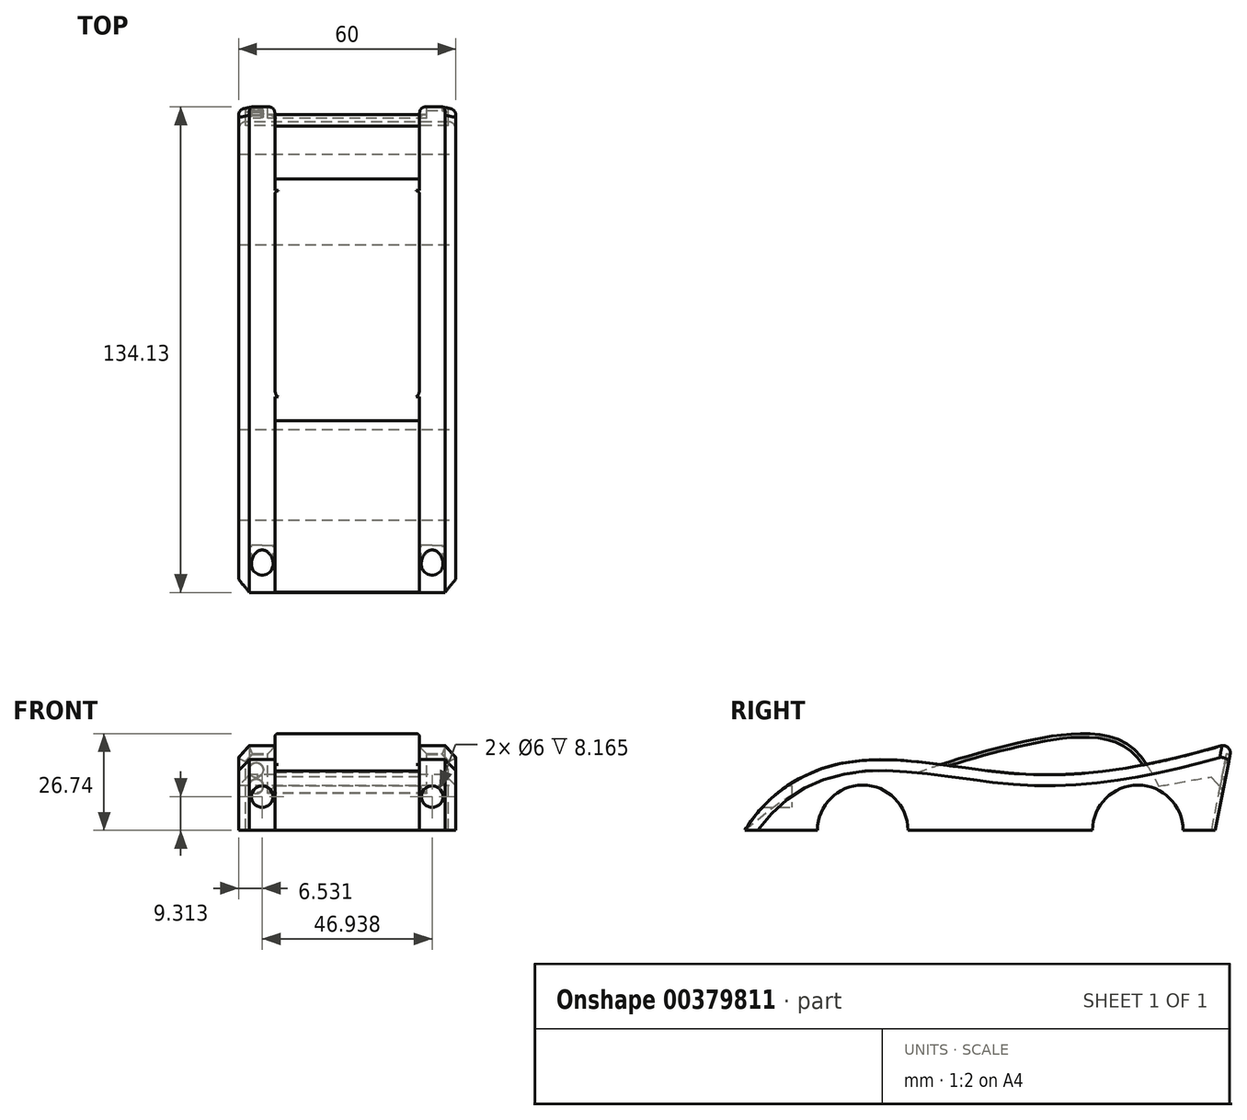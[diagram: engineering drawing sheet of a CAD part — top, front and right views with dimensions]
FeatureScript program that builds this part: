
annotation { "Feature Type Name" : "Feature", "Feature Type Description" : "" }
export const myFeature = defineFeature(function(context is Context, id is Id, definition is map)
    precondition{}
    {
        {
            var Q0;
            Q0=qCreatedBy(makeId("Right.planeOp"),FACE);
            var sketch = newSketch(context, id + "F0", { "sketchPlane" : qUnion([Q0])});
            skLineSegment(sketch, "E0", {"start": v(-69.96, 0) * mm, "end": v(60.04, 0) * mm});
            skLineSegment(sketch, "E1", {"start": v(60.04, 0) * mm, "end": v(64.77, 24.27) * mm});
            skFitSpline(sketch, "E2", {"points": [v(-69.96, 0) * mm, v(-38.45, 19.22) * mm, v(8.82, 15.44) * mm, v(64.77, 24.27) * mm], "startDerivative": vector(75.95, 120.9) * mm, "endDerivative": vector(158.07, 47.6) * mm});
            skSolve(sketch);
        }
        {
            var Q0;
            Q0 = qSketchRegion(id + "F0", true);
            extrude(context, id + "F1", {"entities" : qUnion([Q0]), "endBound" : BoundingType.SYMMETRIC, "depth" : 60 * mm});
        }
        {
            var Q0;
            Q0=qCreatedBy(makeId("Right.planeOp"),FACE);
            var sketch = newSketch(context, id + "F2", { "sketchPlane" : qUnion([Q0])});
            skFitSpline(sketch, "E3", {"points": [v(-69.97, 0) * mm, v(-53.13, 11.86) * mm, v(-31.07, 16.37) * mm, v(-7.6, 13.52) * mm], "startDerivative": vector(49.2, 41.7) * mm, "endDerivative": vector(68.07, -12.52) * mm});
            skLineSegment(sketch, "E4", {"start": v(-69.97, 0) * mm, "end": v(-69.97, 23.96) * mm});
            skLineSegment(sketch, "E5", {"start": v(-69.97, 23.96) * mm, "end": v(-35.1, 31.55) * mm});
            skLineSegment(sketch, "E6", {"start": v(-35.1, 31.55) * mm, "end": v(0, 20.64) * mm});
            skLineSegment(sketch, "E7", {"start": v(0, 20.64) * mm, "end": v(-7.6, 13.52) * mm});
            skLineSegment(sketch, "E8", {"start": v(17.32, 20.64) * mm, "end": v(66.9, 28.23) * mm});
            skFitSpline(sketch, "E9", {"points": [v(17.32, 20.64) * mm, v(24.2, 15.06) * mm, v(39.14, 11.62) * mm, v(65.82, 14.59) * mm, v(68.79, 9.84) * mm], "startDerivative": vector(30.48, -28.51) * mm, "endDerivative": vector(7.56, -36.36) * mm});
            skLineSegment(sketch, "E10", {"start": v(66.9, 28.23) * mm, "end": v(65.82, 14.59) * mm});
            skSolve(sketch);
        }
        {
            var Q0;
            Q0=makeQuery(id+"F2.imprint","IMPRINT",FACE,{"disambiguationData":[TD([[makeQuery(id+"F2.imprint","IMPRINT",EDGE,{"derivedFrom":sQuery(id+"F2.wireOp",EDGE,"E3")}),1.0]])]});
            var Q1;
            {var subQ0=sQuery(id+"F2.wireOp",EDGE,"E8");Q1=makeQuery(id+"F2.imprint","IMPRINT",FACE,{"disambiguationData":[TD([[makeQuery(id+"F2.imprint","IMPRINT",EDGE,{"derivedFrom":subQ0}),-1.0]])]});}
            extrude(context, id + "F3", {"entities" : qUnion([Q0, Q1]), "operationType" : NewBodyOperationType.REMOVE, "endBound" : BoundingType.SYMMETRIC, "depth" : 40 * mm});
        }
        {
            var Q0;
            Q0=qCreatedBy(makeId("Right.planeOp"),FACE);
            var sketch = newSketch(context, id + "F4", { "sketchPlane" : qUnion([Q0])});
            skFitSpline(sketch, "E11", {"points": [v(-24.28, 15.25) * mm, v(3.4, 23.64) * mm, v(35.77, 23.8) * mm, v(46.97, 6.64) * mm], "startDerivative": vector(69.15, 25.57) * mm, "endDerivative": vector(25.04, -44.14) * mm});
            skLineSegment(sketch, "E12", {"start": v(-24.28, 15.25) * mm, "end": v(46.97, 6.64) * mm});
            skSolve(sketch);
        }
        {
            var Q0;
            Q0=makeQuery(id+"F4.imprint","IMPRINT",FACE,{"disambiguationData":[TD([[makeQuery(id+"F4.imprint","IMPRINT",EDGE,{"derivedFrom":sQuery(id+"F4.wireOp",EDGE,"E11")}),-1.0]])]});
            extrude(context, id + "F5", {"entities" : qUnion([Q0]), "operationType" : NewBodyOperationType.ADD, "endBound" : BoundingType.SYMMETRIC, "depth" : 40 * mm});
        }
        {
            var Q0;
            Q0=makeQuery(id+"F1.opExtrude","CAP_EDGE",EDGE,{"disambiguationData":[OSD([sQuery(id+"F0.wireOp",EDGE,"E2")])],"isStart":false});
            var Q1;
            Q1=makeQuery(id+"F1.opExtrude","CAP_EDGE",EDGE,{"disambiguationData":[OSD([sQuery(id+"F0.wireOp",EDGE,"E2")])],"isStart":true});
            var Q2;
            Q2=makeQuery(id+"F3.boolean.opBoolean","INTERSECT",EDGE,{"derivedFrom":[makeQuery(id+"F1.opExtrude","SWEPT_FACE",FACE,{"disambiguationData":[OSD([sQuery(id+"F0.wireOp",EDGE,"E1")])]}),makeQuery(id+"F3.opExtrude","SWEPT_FACE",FACE,{"disambiguationData":[OSD([sQuery(id+"F2.wireOp",EDGE,"E9")])]})]});
            chamfer(context, id + "F6", {"entities" : qUnion([Q0, Q1, Q2]), "width" : 3 * mm, "tangentPropagation" : true});
        }
        {
            var Q0;
            Q0=makeQuery(id+"F3.boolean.opBoolean","INTERSECT",EDGE,{"derivedFrom":[makeQuery(id+"F1.opExtrude","SWEPT_FACE",FACE,{"disambiguationData":[OSD([sQuery(id+"F0.wireOp",EDGE,"E1")])]}),makeQuery(id+"F3.opExtrude","CAP_FACE",FACE,{"disambiguationData":[OSD([sQuery(id+"F2.wireOp",EDGE,"E8"),sQuery(id+"F2.wireOp",EDGE,"E9"),sQuery(id+"F2.wireOp",EDGE,"E10")])],"isStart":false})]});
            var Q1;
            Q1=makeQuery(id+"F3.boolean.opBoolean","INTERSECT",EDGE,{"derivedFrom":[makeQuery(id+"F1.opExtrude","SWEPT_FACE",FACE,{"disambiguationData":[OSD([sQuery(id+"F0.wireOp",EDGE,"E1")])]}),makeQuery(id+"F3.opExtrude","CAP_FACE",FACE,{"disambiguationData":[OSD([sQuery(id+"F2.wireOp",EDGE,"E8"),sQuery(id+"F2.wireOp",EDGE,"E9"),sQuery(id+"F2.wireOp",EDGE,"E10")])],"isStart":true})]});
            var Q2;
            Q2=makeQuery(id+"F6.opChamfer","BLEND_EDGE",EDGE,{"blendedFrom":[makeQuery(id+"F1.opExtrude","CAP_EDGE",EDGE,{"disambiguationData":[OSD([sQuery(id+"F0.wireOp",EDGE,"E2")])],"isStart":true}),makeQuery(id+"F1.opExtrude","SWEPT_FACE",FACE,{"disambiguationData":[OSD([sQuery(id+"F0.wireOp",EDGE,"E1")])]})],"blendedInto":[makeQuery(id+"F1.opExtrude","SWEPT_FACE",FACE,{"disambiguationData":[OSD([sQuery(id+"F0.wireOp",EDGE,"E1")])]})]});
            var Q3;
            {var subQ0=sQuery(id+"F0.wireOp",EDGE,"E2");var subQ1=sQuery(id+"F0.wireOp",EDGE,"E1");Q3=makeQuery(id+"F3.boolean.opBoolean","SPLIT",EDGE,{"disambiguationData":[TD([makeQuery(id+"F3.opExtrude","CAP_FACE",FACE,{"disambiguationData":[OSD([sQuery(id+"F2.wireOp",EDGE,"E8"),sQuery(id+"F2.wireOp",EDGE,"E9"),sQuery(id+"F2.wireOp",EDGE,"E10")])],"isStart":true})])],"derivedFrom":makeQuery(id+"F1.opExtrude","SWEPT_EDGE",EDGE,{"disambiguationData":[OSD([subQ1,subQ0])]})});}
            var Q4;
            {var subQ0=sQuery(id+"F0.wireOp",EDGE,"E2");var subQ1=sQuery(id+"F0.wireOp",EDGE,"E1");Q4=makeQuery(id+"F3.boolean.opBoolean","SPLIT",EDGE,{"disambiguationData":[TD([makeQuery(id+"F3.opExtrude","CAP_FACE",FACE,{"disambiguationData":[OSD([sQuery(id+"F2.wireOp",EDGE,"E8"),sQuery(id+"F2.wireOp",EDGE,"E9"),sQuery(id+"F2.wireOp",EDGE,"E10")])],"isStart":false})])],"derivedFrom":makeQuery(id+"F1.opExtrude","SWEPT_EDGE",EDGE,{"disambiguationData":[OSD([subQ1,subQ0])]})});}
            var Q5;
            Q5=makeQuery(id+"F6.opChamfer","BLEND_EDGE",EDGE,{"blendedFrom":[makeQuery(id+"F1.opExtrude","CAP_EDGE",EDGE,{"disambiguationData":[OSD([sQuery(id+"F0.wireOp",EDGE,"E2")])],"isStart":false}),makeQuery(id+"F1.opExtrude","SWEPT_FACE",FACE,{"disambiguationData":[OSD([sQuery(id+"F0.wireOp",EDGE,"E1")])]})],"blendedInto":[makeQuery(id+"F1.opExtrude","SWEPT_FACE",FACE,{"disambiguationData":[OSD([sQuery(id+"F0.wireOp",EDGE,"E1")])]})]});
            var Q6;
            {var subQ0=makeQuery(id+"F1.opExtrude","SWEPT_FACE",FACE,{"disambiguationData":[OSD([sQuery(id+"F0.wireOp",EDGE,"E1")])]});Q6=makeQuery(id+"F6.opChamfer","BLEND_EDGE",EDGE,{"blendedFrom":[makeQuery(id+"F3.boolean.opBoolean","INTERSECT",EDGE,{"derivedFrom":[subQ0,makeQuery(id+"F3.opExtrude","SWEPT_FACE",FACE,{"disambiguationData":[OSD([sQuery(id+"F2.wireOp",EDGE,"E9")])]})]}),subQ0],"blendedInto":[subQ0]});}
            var Q7;
            Q7=makeQuery(id+"F1.opExtrude","CAP_EDGE",EDGE,{"disambiguationData":[OSD([sQuery(id+"F0.wireOp",EDGE,"E1")])],"isStart":true});
            var Q8;
            Q8=makeQuery(id+"F1.opExtrude","CAP_EDGE",EDGE,{"disambiguationData":[OSD([sQuery(id+"F0.wireOp",EDGE,"E1")])],"isStart":false});
            fillet(context, id + "F7", {"entities" : qUnion([Q0, Q1, Q2, Q3, Q4, Q5, Q6, Q7, Q8]), "radius" : 2 * mm, "tangentPropagation" : true, "allowEdgeOverflow" : false});
        }
        {
            var Q0;
            {var subQ0=sQuery(id+"F4.wireOp",EDGE,"E11");Q0=makeQuery(id+"F5.boolean.opBoolean","SPLIT",EDGE,{"disambiguationData":[topologyDisambiguationEdgeConnected([makeQuery(id+"F5.opExtrude","CAP_FACE",FACE,{"disambiguationData":[OSD([subQ0,sQuery(id+"F4.wireOp",EDGE,"E12")])],"isStart":true})])],"derivedFrom":makeQuery(id+"F5.opExtrude","CAP_EDGE",EDGE,{"disambiguationData":[OSD([subQ0])],"isStart":true})});}
            var Q1;
            {var subQ0=sQuery(id+"F4.wireOp",EDGE,"E11");Q1=makeQuery(id+"F5.boolean.opBoolean","SPLIT",EDGE,{"disambiguationData":[topologyDisambiguationEdgeConnected([makeQuery(id+"F5.opExtrude","CAP_FACE",FACE,{"disambiguationData":[OSD([subQ0,sQuery(id+"F4.wireOp",EDGE,"E12")])],"isStart":false})])],"derivedFrom":makeQuery(id+"F5.opExtrude","CAP_EDGE",EDGE,{"disambiguationData":[OSD([subQ0])],"isStart":false})});}
            fillet(context, id + "F8", {"entities" : qUnion([Q0, Q1]), "radius" : 1 * mm, "tangentPropagation" : true, "allowEdgeOverflow" : false});
        }
        {
            var Q0;
            Q0=qCreatedBy(makeId("Right.planeOp"),FACE);
            var sketch = newSketch(context, id + "F9", { "sketchPlane" : qUnion([Q0])});
            skCircle(sketch, "E13", {"center": v(-37.4, 0) * mm, "radius": 12.5 * mm});
            skCircle(sketch, "E14", {"center": v(38.62, 0) * mm, "radius": 12.5 * mm});
            skSolve(sketch);
        }
        {
            var Q0;
            Q0=makeQuery(id+"F9.imprint","IMPRINT",FACE,{"disambiguationData":[TD([[makeQuery(id+"F9.imprint","IMPRINT",EDGE,{"derivedFrom":sQuery(id+"F9.wireOp",EDGE,"E13")}),1.0]])]});
            var Q1;
            Q1=makeQuery(id+"F9.imprint","IMPRINT",FACE,{"disambiguationData":[TD([[makeQuery(id+"F9.imprint","IMPRINT",EDGE,{"derivedFrom":sQuery(id+"F9.wireOp",EDGE,"E14")}),1.0]])]});
            extrude(context, id + "F10", {"entities" : qUnion([Q0, Q1]), "operationType" : NewBodyOperationType.REMOVE, "endBound" : BoundingType.SYMMETRIC, "oppositeDirection" : true, "depth" : 100 * mm});
        }
        {
            var Q0;
            Q0=qCreatedBy(makeId("Front.planeOp"),FACE);
            cPlane(context, id + "F11", {"entities" : qUnion([Q0]), "cplaneType" : CPlaneType.OFFSET, "offset" : 57 * mm, "width" : 150 * mm, "height" : 150 * mm});
        }
        {
            var Q0;
            Q0=qCreatedBy(id+"F11.planeOp",FACE);
            var sketch = newSketch(context, id + "F12", { "sketchPlane" : qUnion([Q0])});
            skCircle(sketch, "E15", {"center": v(-23.47, 9.31) * mm, "radius": 3 * mm});
            skCircle(sketch, "E16.MirrorC", {"center": v(23.47, 9.31) * mm, "radius": 3 * mm});
            skSolve(sketch);
        }
        {
            var Q0;
            Q0 = qSketchRegion(id + "F12", true);
            var Q1;
            Q1=makeQuery(id+"F1.opExtrude","SWEPT_BODY",BODY,{"disambiguationData":[OSD([sQuery(id+"F0.wireOp",EDGE,"E0"),sQuery(id+"F0.wireOp",EDGE,"E1"),sQuery(id+"F0.wireOp",EDGE,"E2")])]});
            extrude(context, id + "F13", {"entities" : qUnion([Q0]), "operationType" : NewBodyOperationType.REMOVE, "endBoundEntityBody" : qUnion([Q1]), "depth" : 15.4 * mm});
        }
        {
            var Q0;
            Q0=makeQuery(id+"F1.opExtrude","SWEPT_FACE",FACE,{"disambiguationData":[OSD([sQuery(id+"F0.wireOp",EDGE,"E1")])]});
            var sketch = newSketch(context, id + "F14", { "sketchPlane" : qUnion([Q0])});
            skLineSegment(sketch, "E17.bottom", {"start": v(9.73, 14.62) * mm, "end": v(-9.73, 14.62) * mm});
            skLineSegment(sketch, "E17.top", {"start": v(9.73, 19.94) * mm, "end": v(-9.73, 19.94) * mm});
            skLineSegment(sketch, "E17.left", {"start": v(9.73, 14.62) * mm, "end": v(9.73, 19.94) * mm});
            skLineSegment(sketch, "E17.right", {"start": v(-9.73, 14.62) * mm, "end": v(-9.73, 19.94) * mm});
            skPoint(sketch, "E17.middle", {"position": v(0, 17.28) * mm});
            skSolve(sketch);
        }
        {
            var Q0;
            Q0=makeQuery(id+"F14.imprint","IMPRINT",FACE,{"disambiguationData":[TD([[makeQuery(id+"F14.imprint","IMPRINT",EDGE,{"derivedFrom":sQuery(id+"F14.wireOp",EDGE,"E17.bottom")}),-1.0]])]});
            extrude(context, id + "F15", {"entities" : qUnion([Q0]), "operationType" : NewBodyOperationType.REMOVE, "oppositeDirection" : true, "depth" : 1 * mm});
        }
        {
            var Q0;
            Q0=makeQuery(id+"F1.opExtrude","SWEPT_FACE",FACE,{"disambiguationData":[OSD([sQuery(id+"F0.wireOp",EDGE,"E1")])]});
            var sketch = newSketch(context, id + "F16", { "sketchPlane" : qUnion([Q0])});
            skCircle(sketch, "E18", {"center": v(-25.14, 28.4) * mm, "radius": 2 * mm});
            skCircle(sketch, "E19", {"center": v(-25.14, 23.81) * mm, "radius": 2 * mm});
            skCircle(sketch, "E20.MirrorC", {"center": v(25.14, 28.4) * mm, "radius": 2 * mm});
            skCircle(sketch, "E21.MirrorC", {"center": v(25.14, 23.81) * mm, "radius": 2 * mm});
            skSolve(sketch);
        }
        {
            var Q0;
            Q0=makeQuery(id+"F16.imprint","IMPRINT",FACE,{"disambiguationData":[TD([[makeQuery(id+"F16.imprint","IMPRINT",EDGE,{"derivedFrom":sQuery(id+"F16.wireOp",EDGE,"E18")}),1.0]])]});
            var Q1;
            Q1=makeQuery(id+"F16.imprint","IMPRINT",FACE,{"disambiguationData":[TD([[makeQuery(id+"F16.imprint","IMPRINT",EDGE,{"derivedFrom":sQuery(id+"F16.wireOp",EDGE,"E19")}),1.0]])]});
            var Q2;
            Q2=makeQuery(id+"F16.imprint","IMPRINT",FACE,{"disambiguationData":[TD([[makeQuery(id+"F16.imprint","IMPRINT",EDGE,{"derivedFrom":sQuery(id+"F16.wireOp",EDGE,"E20.MirrorC")}),-1.0]])]});
            var Q3;
            Q3=makeQuery(id+"F16.imprint","IMPRINT",FACE,{"disambiguationData":[TD([[makeQuery(id+"F16.imprint","IMPRINT",EDGE,{"derivedFrom":sQuery(id+"F16.wireOp",EDGE,"E21.MirrorC")}),-1.0]])]});
            extrude(context, id + "F17", {"entities" : qUnion([Q0, Q1, Q2, Q3]), "operationType" : NewBodyOperationType.REMOVE, "endBound" : BoundingType.SYMMETRIC, "oppositeDirection" : true, "depth" : 2 * mm});
        }
    });
